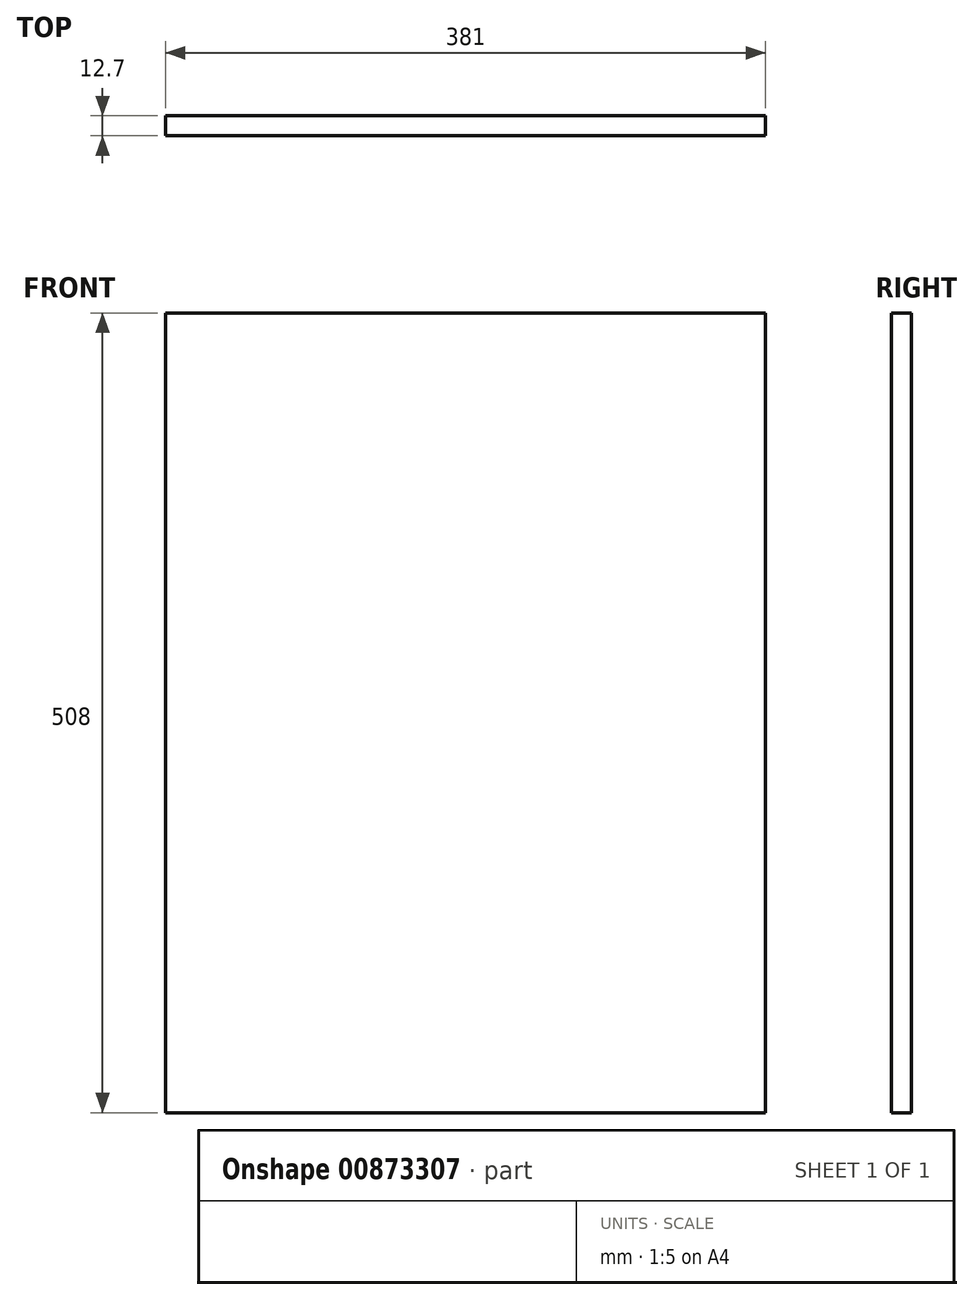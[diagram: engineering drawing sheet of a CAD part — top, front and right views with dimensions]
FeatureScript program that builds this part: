
annotation { "Feature Type Name" : "Feature", "Feature Type Description" : "" }
export const myFeature = defineFeature(function(context is Context, id is Id, definition is map)
    precondition{}
    {
        {
            var Q0;
            Q0=qCreatedBy(makeId("Front.planeOp"),FACE);
            var sketch = newSketch(context, id + "F0", { "sketchPlane" : qUnion([Q0])});
            skLineSegment(sketch, "E0.bottom", {"start": v(0, 0) * mm, "end": v(-381, 0) * mm});
            skLineSegment(sketch, "E0.top", {"start": v(0, 508) * mm, "end": v(-381, 508) * mm});
            skLineSegment(sketch, "E0.left", {"start": v(0, 0) * mm, "end": v(0, 508) * mm});
            skLineSegment(sketch, "E0.right", {"start": v(-381, 0) * mm, "end": v(-381, 508) * mm});
            skSolve(sketch);
        }
        {
            var Q0;
            Q0=makeQuery(id+"F0.imprint","IMPRINT",FACE,{"disambiguationData":[TD([[makeQuery(id+"F0.imprint","IMPRINT",EDGE,{"derivedFrom":sQuery(id+"F0.wireOp",EDGE,"E0.bottom")}),-1.0]])]});
            extrude(context, id + "F1", {"entities" : qUnion([Q0]), "depth" : 12.7 * mm, "offsetDistance" : 25.4 * mm});
        }
    });
